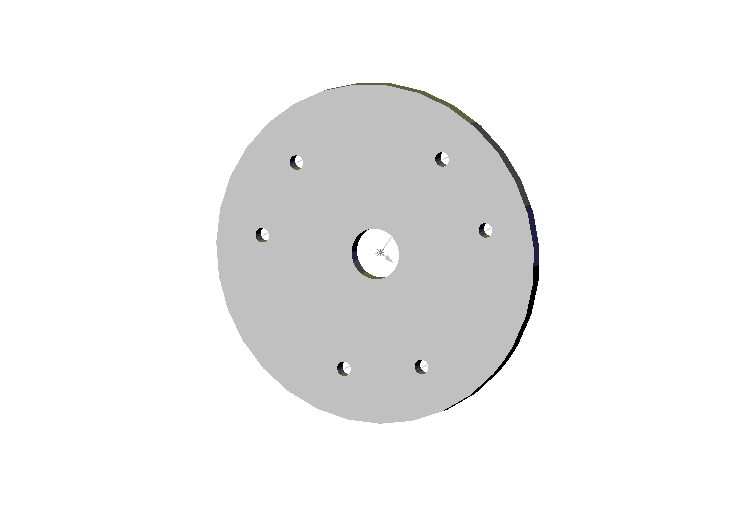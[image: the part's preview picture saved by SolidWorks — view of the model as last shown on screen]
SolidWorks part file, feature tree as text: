
SOLIDWORKS PART (.sldprt)
format: sldprt  version: not decoded by parser v0  size: 113,152 bytes
history: native  units: mm
features: plane x3, sketch x3, pattern_circular x3, cut_extrude x2, extrude x1 (+5 scaffold rows collapsed)
feature tree (17):
  scaffold x5  (default folders/planes/origin — collapsed)
  plane  "Plane1"
  plane  "Plane2"
  plane  "Plane3"
  sketch  "Sketch1"  dims[D1=70.0mm]
  extrude  "Base-Extrude"  Depth=3mm
  sketch  "Sketch2"  dims[D1=10.5mm]
  cut_extrude  "Cut-Extrude1"  [1 undecoded]
  sketch  "Sketch4"  dims[D1=3.0mm D2=25.0mm]
  cut_extrude  "Cut-Extrude4"  [1 undecoded]
  pattern_circular  "CirPattern3"  Count=2 Angle=40deg
  pattern_circular  "CirPattern4"  Count=2 Angle=120deg
  pattern_circular  "CirPattern6"  Count=2 Angle=120deg
decode coverage: 7 of 9 modeling features carry decoded parameters
note: 2 parameter values undecoded
note: suppression state not decoded; provenance and decode notes live in map.json
